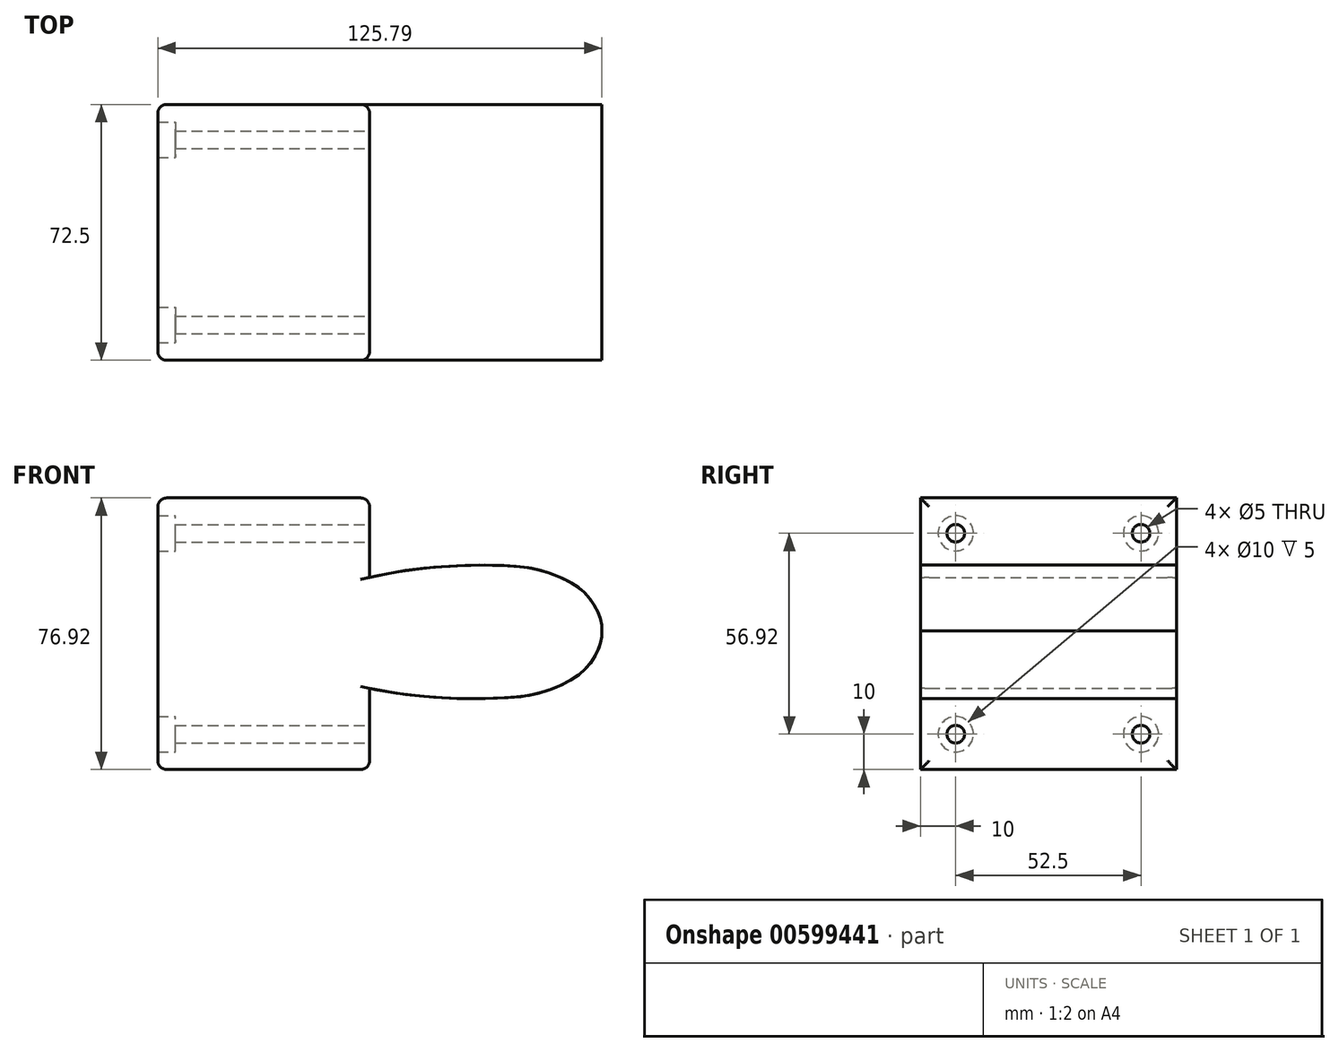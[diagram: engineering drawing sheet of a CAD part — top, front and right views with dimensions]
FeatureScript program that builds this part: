
annotation { "Feature Type Name" : "Feature", "Feature Type Description" : "" }
export const myFeature = defineFeature(function(context is Context, id is Id, definition is map)
    precondition{}
    {
        {
            var Q0;
            Q0=qCreatedBy(makeId("Front.planeOp"),FACE);
            var sketch = newSketch(context, id + "F0", { "sketchPlane" : qUnion([Q0]), "disableImprinting" : false});
            skFitSpline(sketch, "E0.0", {"points": [v(-56.59, 0.04) * mm, v(-55.54, 0.85) * mm, v(-53.18, 2.44) * mm, v(-49, 4.79) * mm, v(-44.32, 7.05) * mm, v(-39.28, 9.2) * mm, v(-34.03, 11.2) * mm, v(-29.6, 12.7) * mm, v(-26.1, 13.78) * mm, v(-22.66, 14.76) * mm, v(-18.46, 15.83) * mm, v(-13.6, 16.88) * mm, v(-7.4, 18) * mm, v(-1.56, 18.74) * mm, v(3.83, 19.2) * mm, v(7.67, 19.44) * mm, v(11.33, 19.58) * mm, v(14.83, 19.62) * mm, v(17.61, 19.6) * mm, v(19.78, 19.56) * mm, v(21.92, 19.49) * mm, v(24.55, 19.33) * mm, v(27.14, 19.04) * mm, v(29.2, 18.69) * mm, v(30.73, 18.36) * mm, v(32.25, 17.95) * mm, v(34.23, 17.33) * mm, v(36.6, 16.42) * mm, v(38.75, 15.39) * mm, v(40.3, 14.52) * mm, v(41.36, 13.85) * mm, v(42.34, 13.16) * mm, v(43.26, 12.42) * mm, v(44.1, 11.62) * mm, v(44.9, 10.76) * mm, v(45.63, 9.83) * mm, v(46.32, 8.84) * mm, v(46.96, 7.8) * mm, v(47.53, 6.73) * mm, v(47.93, 5.84) * mm, v(48.2, 5.12) * mm, v(48.38, 4.58) * mm, v(48.52, 4.05) * mm, v(48.66, 3.37) * mm, v(48.77, 2.58) * mm, v(48.81, 1.73) * mm, v(48.82, 1.25) * mm, v(48.83, 1.03) * mm]});
            skFitSpline(sketch, "E0.1", {"points": [v(-56.59, 0.04) * mm, v(-55.52, -0.74) * mm, v(-53.13, -2.3) * mm, v(-48.9, -4.56) * mm, v(-44.19, -6.73) * mm, v(-39.1, -8.8) * mm, v(-33.82, -10.69) * mm, v(-29.36, -12.1) * mm, v(-25.85, -13.11) * mm, v(-22.38, -14.03) * mm, v(-18.17, -15.02) * mm, v(-13.3, -15.98) * mm, v(-7.06, -16.98) * mm, v(-1.22, -17.6) * mm, v(4.19, -17.98) * mm, v(8.03, -18.14) * mm, v(11.7, -18.2) * mm, v(15.19, -18.18) * mm, v(17.97, -18.1) * mm, v(20.13, -18.02) * mm, v(22.27, -17.91) * mm, v(24.9, -17.7) * mm, v(27.49, -17.36) * mm, v(29.54, -16.97) * mm, v(31.06, -16.62) * mm, v(32.57, -16.18) * mm, v(34.54, -15.52) * mm, v(36.9, -14.56) * mm, v(39.02, -13.5) * mm, v(40.55, -12.6) * mm, v(41.6, -11.9) * mm, v(42.58, -11.2) * mm, v(43.48, -10.44) * mm, v(44.3, -9.62) * mm, v(45.08, -8.75) * mm, v(45.8, -7.8) * mm, v(46.47, -6.8) * mm, v(47.09, -5.75) * mm, v(47.64, -4.67) * mm, v(48.02, -3.77) * mm, v(48.28, -3.05) * mm, v(48.45, -2.5) * mm, v(48.58, -1.97) * mm, v(48.7, -1.29) * mm, v(48.8, -0.5) * mm, v(48.83, 0.35) * mm, v(48.83, 0.83) * mm, v(48.83, 1.06) * mm]});
            skLineSegment(sketch, "E1", {"start": v(-16.96, 16.14) * mm, "end": v(-16.96, 38.67) * mm});
            skLineSegment(sketch, "E2", {"start": v(-16.96, 38.67) * mm, "end": v(-76.96, 38.67) * mm});
            skLineSegment(sketch, "E3", {"start": v(-76.96, 38.67) * mm, "end": v(-76.96, -38.25) * mm});
            skLineSegment(sketch, "E4", {"start": v(-76.96, -38.25) * mm, "end": v(-16.96, -38.25) * mm});
            skLineSegment(sketch, "E5", {"start": v(-16.96, -38.25) * mm, "end": v(-16.96, -15.25) * mm});
            skSolve(sketch);
        }
        {
            var Q0;
            Q0 = qSketchRegion(id + "F0", true);
            extrude(context, id + "F1", {"entities" : qUnion([Q0]), "depth" : 72.5 * mm, "offsetDistance" : 25 * mm});
        }
        {
            var Q0;
            Q0=makeQuery(id+"F1.opExtrude","SWEPT_FACE",FACE,{"disambiguationData":[OSD([sQuery(id+"F0.wireOp",EDGE,"E3")])]});
            var sketch = newSketch(context, id + "F2", { "sketchPlane" : qUnion([Q0]), "disableImprinting" : false});
            skLineSegment(sketch, "E6", {"start": v(10, 64.3) * mm, "end": v(10, -67.48) * mm, "construction": true});
            skLineSegment(sketch, "E7", {"start": v(62.5, 65.18) * mm, "end": v(62.5, -67.48) * mm, "construction": true});
            skLineSegment(sketch, "E8", {"start": v(-71.51, -28.25) * mm, "end": v(121.85, -28.25) * mm, "construction": true});
            skLineSegment(sketch, "E9", {"start": v(-71.51, 28.67) * mm, "end": v(123.4, 28.67) * mm, "construction": true});
            skPoint(sketch, "E10", {"position": v(10, 28.67) * mm});
            skPoint(sketch, "E11", {"position": v(62.5, 28.67) * mm});
            skPoint(sketch, "E12", {"position": v(62.5, -28.25) * mm});
            skPoint(sketch, "E13", {"position": v(10, -28.25) * mm});
            skSolve(sketch);
        }
        {
            var Q0;
            Q0=sQuery(id+"F2.wireOp",VERTEX,"E10");
            var Q1;
            Q1=sQuery(id+"F2.wireOp",VERTEX,"E11");
            var Q2;
            Q2=sQuery(id+"F2.wireOp",VERTEX,"E12");
            var Q3;
            Q3=sQuery(id+"F2.wireOp",VERTEX,"E13");
            var Q4;
            Q4=makeQuery(id+"F1.opExtrude","SWEPT_BODY",BODY,{"disambiguationData":[OSD([sQuery(id+"F0.wireOp",EDGE,"E0.0"),sQuery(id+"F0.wireOp",EDGE,"E0.1"),sQuery(id+"F0.wireOp",EDGE,"E1"),sQuery(id+"F0.wireOp",EDGE,"E2"),sQuery(id+"F0.wireOp",EDGE,"E3"),sQuery(id+"F0.wireOp",EDGE,"E4"),sQuery(id+"F0.wireOp",EDGE,"E5")])]});
            hole(context, id + "F3", {"style" : HoleStyle.C_BORE, "endStyle" : HoleEndStyle.THROUGH, "holeDiameter" : 5 * mm, "cBoreDiameter" : 10 * mm, "cBoreDepth" : 5 * mm, "majorDiameter" : 5 * mm, "isTappedThrough" : true, "tappedDepth" : 12 * mm, "tapClearance" : 3, "locations" : qUnion([Q0, Q1, Q2, Q3]), "scope" : qUnion([Q4]), "startStyle" : HoleStartStyle.PART});
        }
        {
            var Q0;
            Q0=makeQuery(id+"F1.opExtrude","CAP_EDGE",EDGE,{"disambiguationData":[OSD([sQuery(id+"F0.wireOp",EDGE,"E3")])],"isStart":false});
            var Q1;
            Q1=makeQuery(id+"F1.opExtrude","SWEPT_EDGE",EDGE,{"disambiguationData":[OSD([sQuery(id+"F0.wireOp",EDGE,"E2"),sQuery(id+"F0.wireOp",EDGE,"E3")])]});
            var Q2;
            Q2=makeQuery(id+"F1.opExtrude","CAP_EDGE",EDGE,{"disambiguationData":[OSD([sQuery(id+"F0.wireOp",EDGE,"E3")])],"isStart":true});
            var Q3;
            Q3=makeQuery(id+"F1.opExtrude","SWEPT_EDGE",EDGE,{"disambiguationData":[OSD([sQuery(id+"F0.wireOp",EDGE,"E3"),sQuery(id+"F0.wireOp",EDGE,"E4")])]});
            fillet(context, id + "F4", {"entities" : qUnion([Q0, Q1, Q2, Q3]), "radius" : 2.5 * mm, "tangentPropagation" : true, "allowEdgeOverflow" : false});
        }
        {
            var Q0;
            Q0=makeQuery(id+"F1.opExtrude","SWEPT_EDGE",EDGE,{"disambiguationData":[OSD([sQuery(id+"F0.wireOp",EDGE,"E1"),sQuery(id+"F0.wireOp",EDGE,"E2")])]});
            var Q1;
            Q1=makeQuery(id+"F1.opExtrude","CAP_EDGE",EDGE,{"disambiguationData":[OSD([sQuery(id+"F0.wireOp",EDGE,"E1")])],"isStart":false});
            var Q2;
            Q2=makeQuery(id+"F1.opExtrude","CAP_EDGE",EDGE,{"disambiguationData":[OSD([sQuery(id+"F0.wireOp",EDGE,"E1")])],"isStart":true});
            var Q3;
            Q3=makeQuery(id+"F1.opExtrude","CAP_EDGE",EDGE,{"disambiguationData":[OSD([sQuery(id+"F0.wireOp",EDGE,"E5")])],"isStart":true});
            var Q4;
            Q4=makeQuery(id+"F1.opExtrude","SWEPT_EDGE",EDGE,{"disambiguationData":[OSD([sQuery(id+"F0.wireOp",EDGE,"E4"),sQuery(id+"F0.wireOp",EDGE,"E5")])]});
            var Q5;
            Q5=makeQuery(id+"F1.opExtrude","CAP_EDGE",EDGE,{"disambiguationData":[OSD([sQuery(id+"F0.wireOp",EDGE,"E5")])],"isStart":false});
            fillet(context, id + "F5", {"entities" : qUnion([Q0, Q1, Q2, Q3, Q4, Q5]), "radius" : 2.5 * mm, "tangentPropagation" : true, "allowEdgeOverflow" : false});
        }
    });
